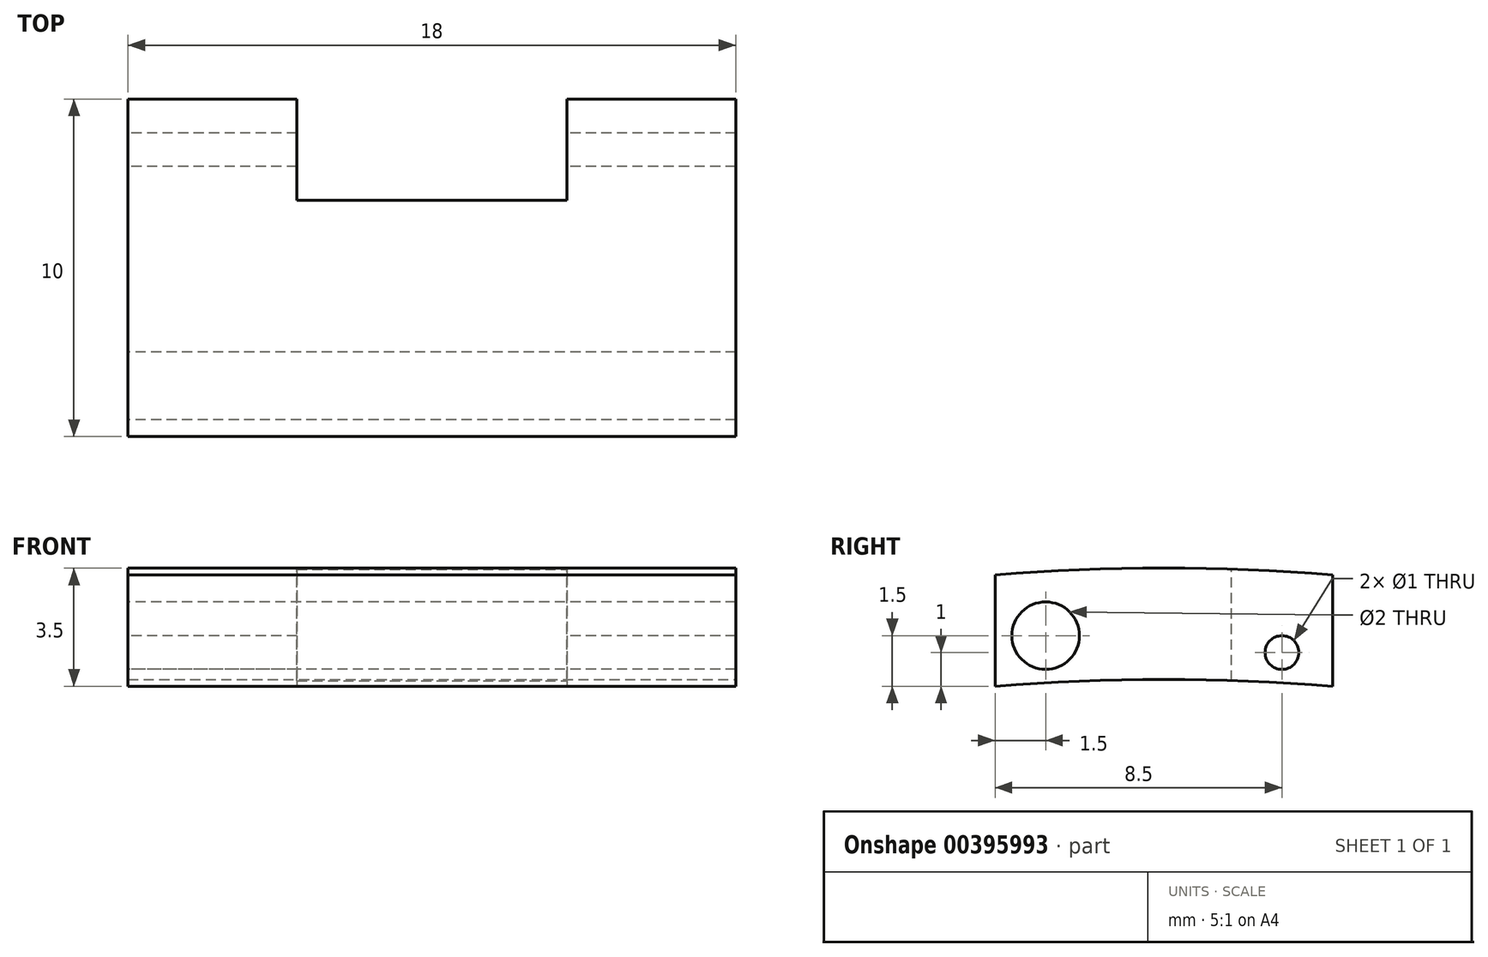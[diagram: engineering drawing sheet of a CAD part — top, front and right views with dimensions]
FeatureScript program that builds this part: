
annotation { "Feature Type Name" : "Feature", "Feature Type Description" : "" }
export const myFeature = defineFeature(function(context is Context, id is Id, definition is map)
    precondition{}
    {
        {
            var Q0;
            Q0=qCreatedBy(makeId("Front.planeOp"),FACE);
            var sketch = newSketch(context, id + "F0", { "sketchPlane" : qUnion([Q0])});
            skLineSegment(sketch, "E0.bottom", {"start": v(-9, -1.75) * mm, "end": v(9, -1.75) * mm});
            skLineSegment(sketch, "E0.top", {"start": v(-9, 1.75) * mm, "end": v(9, 1.75) * mm});
            skLineSegment(sketch, "E0.left", {"start": v(-9, -1.75) * mm, "end": v(-9, 1.75) * mm});
            skLineSegment(sketch, "E0.right", {"start": v(9, -1.75) * mm, "end": v(9, 1.75) * mm});
            skPoint(sketch, "E0.middle", {"position": v(0, 0) * mm});
            skSolve(sketch);
        }
        {
            var Q0;
            Q0 = qSketchRegion(id + "F0", true);
            extrude(context, id + "F1", {"entities" : qUnion([Q0]), "depth" : 10 * mm});
        }
        {
            var Q0;
            Q0=qCreatedBy(makeId("Top.planeOp"),FACE);
            var sketch = newSketch(context, id + "F2", { "sketchPlane" : qUnion([Q0])});
            skLineSegment(sketch, "E1.bottom", {"start": v(-4, 3) * mm, "end": v(4, 3) * mm});
            skLineSegment(sketch, "E1.top", {"start": v(-4, -3) * mm, "end": v(4, -3) * mm});
            skLineSegment(sketch, "E1.left", {"start": v(-4, 3) * mm, "end": v(-4, -3) * mm});
            skLineSegment(sketch, "E1.right", {"start": v(4, 3) * mm, "end": v(4, -3) * mm});
            skPoint(sketch, "E1.middle", {"position": v(0, 0) * mm});
            skSolve(sketch);
        }
        {
            var Q0;
            Q0 = qSketchRegion(id + "F2", true);
            extrude(context, id + "F3", {"entities" : qUnion([Q0]), "operationType" : NewBodyOperationType.REMOVE, "oppositeDirection" : true, "depth" : 25 * mm});
        }
        {
            var Q0;
            Q0 = qSketchRegion(id + "F2", true);
            extrude(context, id + "F4", {"entities" : qUnion([Q0]), "operationType" : NewBodyOperationType.REMOVE, "depth" : 21.2 * mm});
        }
        {
            var Q0;
            Q0=makeQuery(id+"F1.opExtrude","SWEPT_FACE",FACE,{"disambiguationData":[OSD([sQuery(id+"F0.wireOp",EDGE,"E0.right")])]});
            var sketch = newSketch(context, id + "F5", { "sketchPlane" : qUnion([Q0])});
            skLineSegment(sketch, "E2", {"start": v(-5, 1.75) * mm, "end": v(-5, -1.55) * mm});
            skPoint(sketch, "E2.endSnap0", {"position": v(-5, 1.75) * mm});
            skLineSegment(sketch, "E3", {"start": v(-10, -1.75) * mm, "end": v(-10, 1.55) * mm});
            skLineSegment(sketch, "E4", {"start": v(0, -1.75) * mm, "end": v(0, 1.55) * mm});
            skArc(sketch, "E5", {"start": v(0, 1.55) * mm, "mid": v(-5, 1.75) * mm, "end": v(-10, 1.55) * mm});
            skArc(sketch, "E6", {"start": v(0, -1.75) * mm, "mid": v(-5, -1.55) * mm, "end": v(-10, -1.75) * mm});
            skSolve(sketch);
        }
        {
            var Q0;
            Q0 = qSketchRegion(id + "F5", true);
            extrude(context, id + "F6", {"entities" : qUnion([Q0]), "operationType" : NewBodyOperationType.INTERSECT, "oppositeDirection" : true, "depth" : 18 * mm});
        }
        {
            var Q0;
            Q0=makeQuery(id+"F1.opExtrude","SWEPT_FACE",FACE,{"disambiguationData":[OSD([sQuery(id+"F0.wireOp",EDGE,"E0.left")])]});
            var sketch = newSketch(context, id + "F7", { "sketchPlane" : qUnion([Q0])});
            skLineSegment(sketch, "E7", {"start": v(0, -1.75) * mm, "end": v(0, -0.75) * mm});
            skLineSegment(sketch, "E8", {"start": v(0, -0.75) * mm, "end": v(1.5, -0.75) * mm});
            skLineSegment(sketch, "E9", {"start": v(10, -1.75) * mm, "end": v(10, -0.25) * mm});
            skLineSegment(sketch, "E10", {"start": v(10, -0.25) * mm, "end": v(8.5, -0.25) * mm});
            skCircle(sketch, "E11", {"center": v(1.5, -0.75) * mm, "radius": 0.5 * mm});
            skCircle(sketch, "E12", {"center": v(8.5, -0.25) * mm, "radius": 1 * mm});
            skSolve(sketch);
        }
        {
            var Q0;
            Q0 = qSketchRegion(id + "F7", true);
            extrude(context, id + "F8", {"entities" : qUnion([Q0]), "operationType" : NewBodyOperationType.REMOVE, "oppositeDirection" : true, "depth" : 25 * mm});
        }
    });
